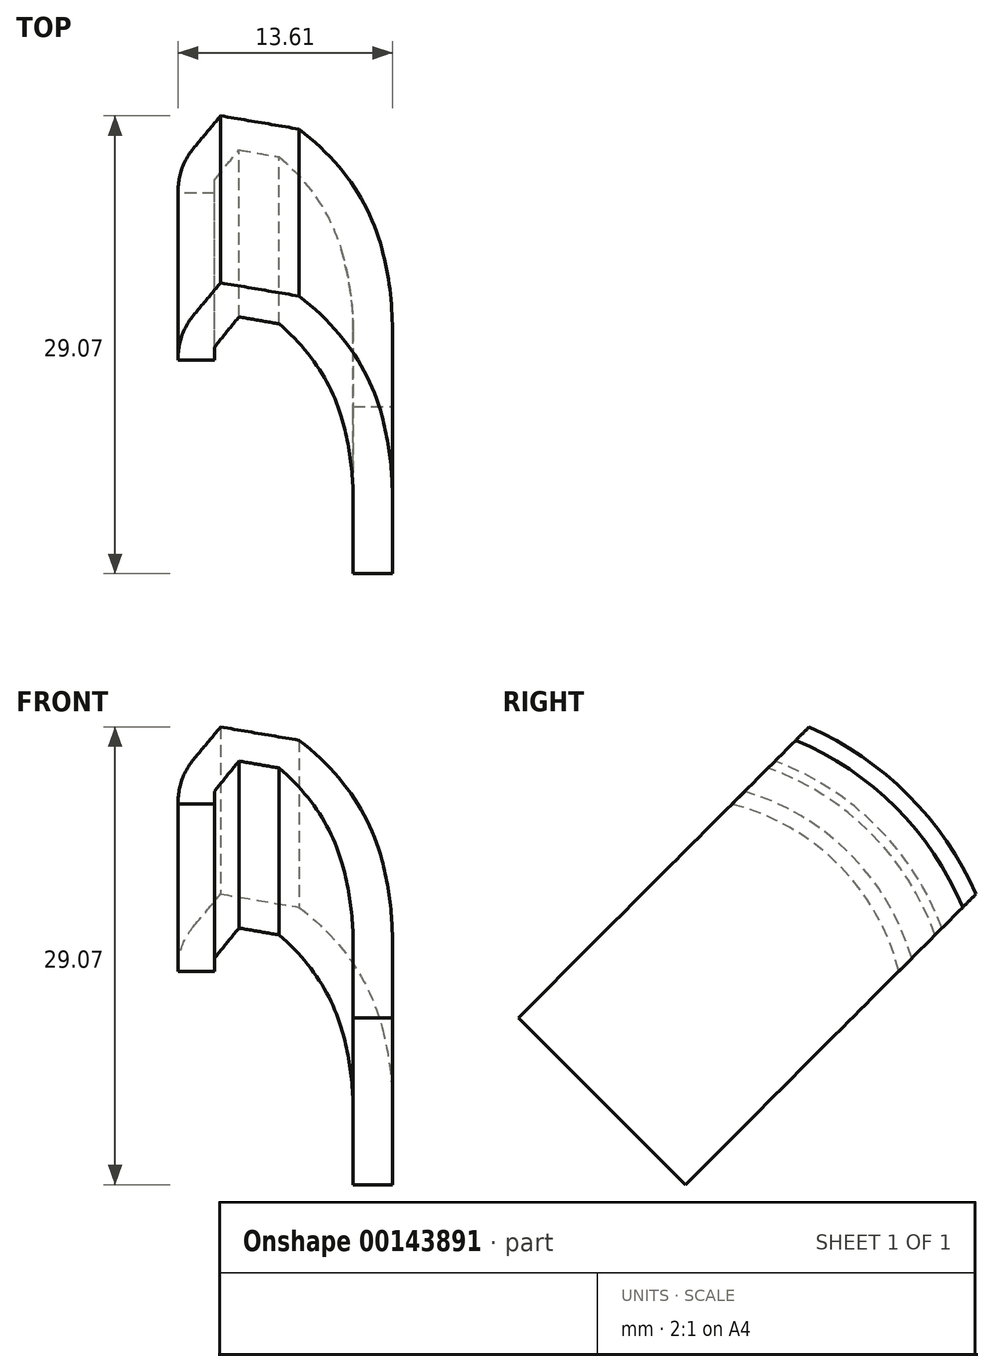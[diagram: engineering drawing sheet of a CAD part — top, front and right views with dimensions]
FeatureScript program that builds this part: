
annotation { "Feature Type Name" : "Feature", "Feature Type Description" : "" }
export const myFeature = defineFeature(function(context is Context, id is Id, definition is map)
    precondition{}
    {
        {
            var Q0;
            Q0=qCreatedBy(makeId("Top.planeOp"),FACE);
            var sketch = newSketch(context, id + "F0", { "sketchPlane" : qUnion([Q0])});
            skLineSegment(sketch, "E0", {"start": v(0, 0) * mm, "end": v(0, 5.47) * mm});
            skArc(sketch, "E1", {"start": v(0, 5.47) * mm, "mid": v(-1.22, 11.92) * mm, "end": v(-4.7, 17.48) * mm});
            skLineSegment(sketch, "E2", {"start": v(-4.7, 17.48) * mm, "end": v(-7.25, 18.04) * mm});
            skLineSegment(sketch, "E3", {"start": v(-7.25, 18.04) * mm, "end": v(-8.8, 15.6) * mm});
            skLineSegment(sketch, "E4.0", {"start": v(-8.41, 20.86) * mm, "end": v(-10.13, 18.18) * mm});
            skLineSegment(sketch, "E4.1", {"start": v(-3.43, 19.76) * mm, "end": v(-8.41, 20.86) * mm});
            skArc(sketch, "E4.2", {"start": v(2.5, 5.47) * mm, "mid": v(0.96, 13.2) * mm, "end": v(-3.43, 19.76) * mm});
            skLineSegment(sketch, "E4.3", {"start": v(2.5, 0) * mm, "end": v(2.5, 5.47) * mm});
            skLineSegment(sketch, "E5", {"start": v(0, 0) * mm, "end": v(2.5, 0) * mm});
            skLineSegment(sketch, "E6", {"start": v(-8.8, 15.6) * mm, "end": v(-10.13, 18.18) * mm, "construction": true});
            skLineSegment(sketch, "E7", {"start": v(-8.8, 15.6) * mm, "end": v(-8.8, 14.6) * mm});
            skLineSegment(sketch, "E8", {"start": v(-8.8, 14.6) * mm, "end": v(-11.1, 14.6) * mm});
            skArc(sketch, "E9", {"start": v(-10.13, 18.18) * mm, "mid": v(-10.88, 16.47) * mm, "end": v(-11.1, 14.6) * mm});
            skSolve(sketch);
        }
        {
            var Q0;
            Q0=makeQuery(id+"F0.imprint","IMPRINT",FACE,{"disambiguationData":[TD([[makeQuery(id+"F0.imprint","IMPRINT",EDGE,{"derivedFrom":sQuery(id+"F0.wireOp",EDGE,"E0")}),-1.0]])]});
            var Q1;
            Q1=sQuery(id+"F0.wireOp",EDGE,"E5");
            revolve(context, id + "F1", {"entities" : qUnion([Q0]), "axis" : qUnion([Q1]), "revolveType" : RevolveType.ONE_DIRECTION, "angle" : 90 * degree});
        }
        {
            assignVariable(context, id + "F2", {"name" : "size", "anyValue" : 10});
        }
        {
            var Q0;
            Q0=makeQuery(id+"F1.opRevolve","CAP_FACE",FACE,{"disambiguationData":[OSD([sQuery(id+"F0.wireOp",EDGE,"E0"),sQuery(id+"F0.wireOp",EDGE,"E1"),sQuery(id+"F0.wireOp",EDGE,"E2"),sQuery(id+"F0.wireOp",EDGE,"E3"),sQuery(id+"F0.wireOp",EDGE,"E4.0"),sQuery(id+"F0.wireOp",EDGE,"E4.1"),sQuery(id+"F0.wireOp",EDGE,"E4.2"),sQuery(id+"F0.wireOp",EDGE,"E4.3"),sQuery(id+"F0.wireOp",EDGE,"E5"),sQuery(id+"F0.wireOp",EDGE,"E7"),sQuery(id+"F0.wireOp",EDGE,"E8"),sQuery(id+"F0.wireOp",EDGE,"E9")])],"isStart":true});
            extrude(context, id + "F3", {"entities" : qUnion([Q0]), "operationType" : NewBodyOperationType.ADD, "depth" : (getVariable(context, 'size')) * mm});
        }
        {
            var Q0;
            {var subQ0=sQuery(id+"F0.wireOp",EDGE,"E5");Q0=makeQuery(id+"F3.boolean.opBoolean","MERGE",FACE,{"derivedFrom":[makeQuery(id+"F1.opRevolve","CAP_FACE",FACE,{"disambiguationData":[OSD([sQuery(id+"F0.wireOp",EDGE,"E0"),sQuery(id+"F0.wireOp",EDGE,"E1"),sQuery(id+"F0.wireOp",EDGE,"E2"),sQuery(id+"F0.wireOp",EDGE,"E3"),sQuery(id+"F0.wireOp",EDGE,"E4.0"),sQuery(id+"F0.wireOp",EDGE,"E4.1"),sQuery(id+"F0.wireOp",EDGE,"E4.2"),sQuery(id+"F0.wireOp",EDGE,"E4.3"),subQ0,sQuery(id+"F0.wireOp",EDGE,"E7"),sQuery(id+"F0.wireOp",EDGE,"E8"),sQuery(id+"F0.wireOp",EDGE,"E9")])],"isStart":false}),makeQuery(id+"F3.opExtrude","SWEPT_FACE",FACE,{"disambiguationData":[OSD([subQ0])]})]});}
            extrude(context, id + "F4", {"entities" : qUnion([Q0]), "operationType" : NewBodyOperationType.ADD, "depth" : (getVariable(context, 'size')) * mm});
        }
        {
            var Q0;
            {var subQ0=sQuery(id+"F0.wireOp",EDGE,"E4.3");Q0=makeQuery(id+"F4.boolean.opBoolean","MERGE",FACE,{"derivedFrom":[makeQuery(id+"F3.boolean.opBoolean","MERGE",FACE,{"derivedFrom":[makeQuery(id+"F1.opRevolve","SWEPT_FACE",FACE,{"disambiguationData":[OSD([subQ0])]}),makeQuery(id+"F3.opExtrude","SWEPT_FACE",FACE,{"disambiguationData":[OSD([subQ0])]})]}),makeQuery(id+"F4.opExtrude","SWEPT_FACE",FACE,{"disambiguationData":[OSD([subQ0,sQuery(id+"F0.wireOp",EDGE,"E5")])]})]});}
            var sketch = newSketch(context, id + "F5", { "sketchPlane" : qUnion([Q0])});
            skLineSegment(sketch, "E10", {"start": v(-10, 0.6) * mm, "end": v(0.6, -10) * mm});
            skLineSegment(sketch, "E11", {"start": v(0.6, -10) * mm, "end": v(23.04, 12.44) * mm});
            skLineSegment(sketch, "E12", {"start": v(23.04, 12.44) * mm, "end": v(12.44, 23.04) * mm});
            skLineSegment(sketch, "E13", {"start": v(12.44, 23.04) * mm, "end": v(-10, 0.6) * mm});
            skLineSegment(sketch, "E14", {"start": v(-10, 0.6) * mm, "end": v(-10, -10) * mm, "construction": true});
            skLineSegment(sketch, "E15", {"start": v(-10, -10) * mm, "end": v(0.6, -10) * mm, "construction": true});
            skSolve(sketch);
        }
        {
            var Q0;
            Q0 = qSketchRegion(id + "F5", true);
            extrude(context, id + "F6", {"entities" : qUnion([Q0]), "operationType" : NewBodyOperationType.INTERSECT, "oppositeDirection" : true, "depth" : 25 * mm});
        }
        {
            var Q0;
            Q0=qCreatedBy(makeId("Right.planeOp"),FACE);
            cPlane(context, id + "F7", {"entities" : qUnion([Q0]), "cplaneType" : CPlaneType.OFFSET, "offset" : 25 * mm, "width" : 150 * mm, "height" : 150 * mm});
        }
    });
